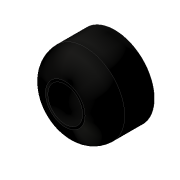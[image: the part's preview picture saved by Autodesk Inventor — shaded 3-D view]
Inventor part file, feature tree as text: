
AUTODESK INVENTOR PART (.ipt)
format: ipt  version: 2017 (Build 210142000, 142)  size: 115,712 bytes
history: native  units: in
note: dims shown in document units (in); Inventor stores cm internally (conversion verified against a paired STEP export)
features: revolve x1, sketch x1
ambient origin geometry x8: Origin, YZ Plane, XZ Plane, XY Plane, X Axis, Y Axis, Z Axis, Center Point
bodies: Solid1 (feature_tree)
feature tree (2):
  revolve  "Revolution1"  [1 undecoded]
  sketch  "Sketch1"  dims[d0=0.1in d1=0.2in d2=0.25in d3=0.0625in d4=90.0deg d5=0.05in]
note: 1 required parameter value undecoded (feature->parameter linkage not recoverable at this tier; creation-order binding heuristic only, values carry confidence <= 0.55)
